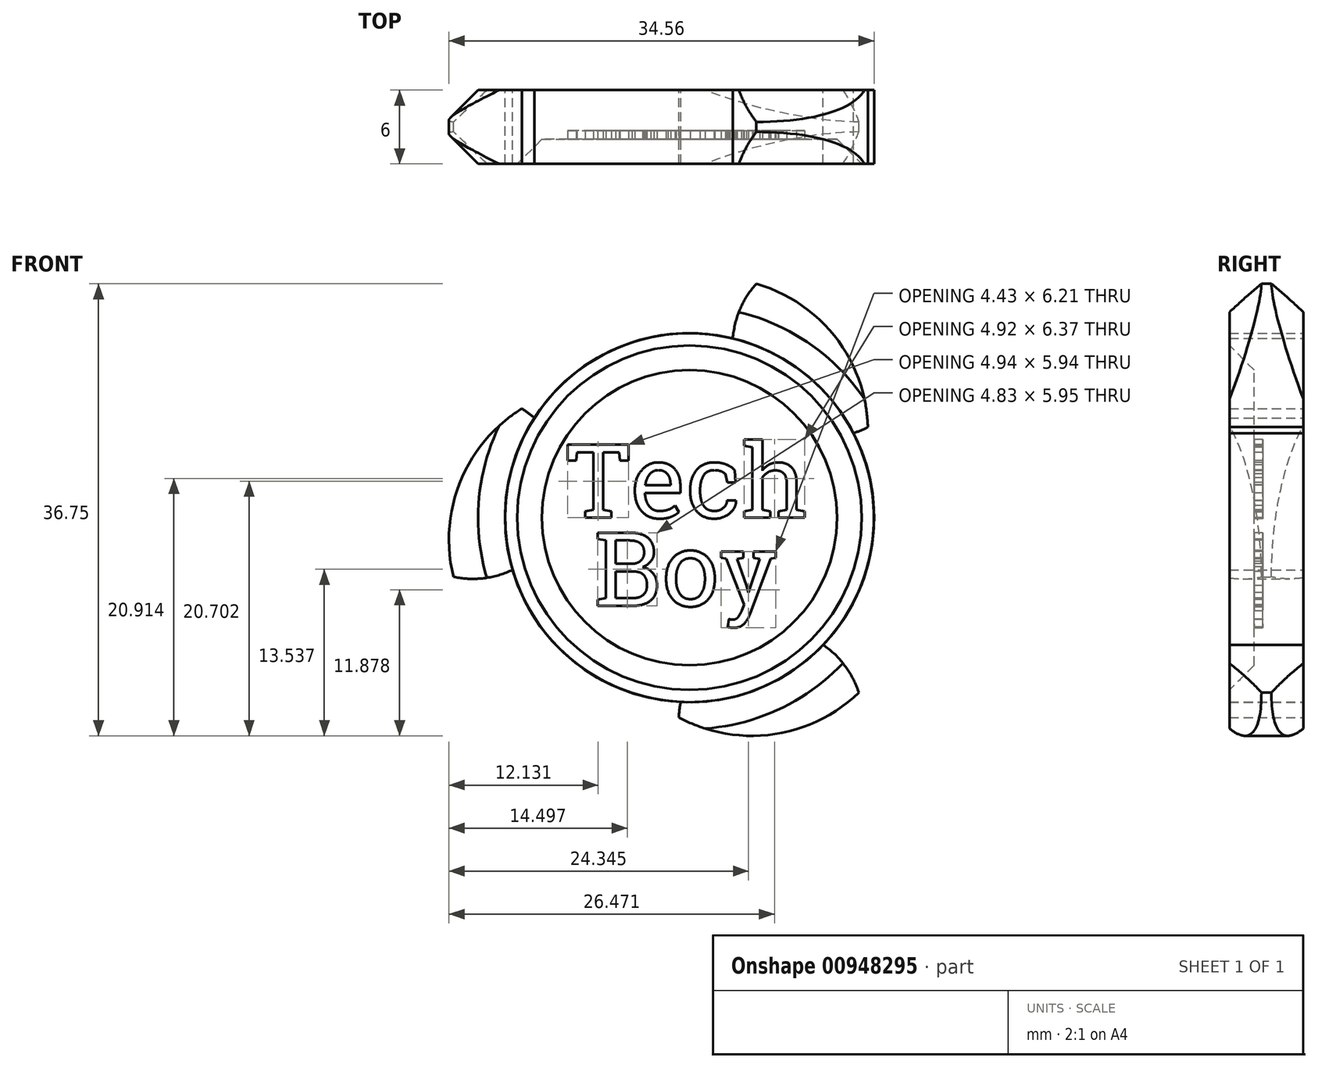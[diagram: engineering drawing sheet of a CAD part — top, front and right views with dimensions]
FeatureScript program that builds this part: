
annotation { "Feature Type Name" : "Feature", "Feature Type Description" : "" }
export const myFeature = defineFeature(function(context is Context, id is Id, definition is map)
    precondition{}
    {
        {
            var Q0;
            Q0=qCreatedBy(makeId("Front.planeOp"),FACE);
            var sketch = newSketch(context, id + "F0", { "sketchPlane" : qUnion([Q0])});
            skCircle(sketch, "E0", {"center": v(0, 0) * mm, "radius": 15 * mm});
            skSolve(sketch);
        }
        {
            var Q0;
            Q0=makeQuery(id+"F0.imprint","IMPRINT",FACE,{"disambiguationData":[TD([[makeQuery(id+"F0.imprint","IMPRINT",EDGE,{"derivedFrom":sQuery(id+"F0.wireOp",EDGE,"E0")}),1.0]])]});
            extrude(context, id + "F1", {"entities" : qUnion([Q0]), "depth" : 6 * mm, "offsetDistance" : 25.4 * mm});
        }
        {
            var Q0;
            Q0=qCreatedBy(makeId("Front.planeOp"),FACE);
            var sketch = newSketch(context, id + "F2", { "sketchPlane" : qUnion([Q0])});
            skCircle(sketch, "E1", {"center": v(2, 7) * mm, "radius": 12.5 * mm});
            skCircle(sketch, "E2", {"center": v(11, 14) * mm, "radius": 7.5 * mm});
            skCircle(sketch, "E3.0.0", {"center": v(0, 0) * mm, "radius": 15 * mm});
            skSolve(sketch);
        }
        {
            var Q0;
            {var subQ0=sQuery(id+"F2.wireOp",EDGE,"E2");var subQ1=sQuery(id+"F2.wireOp",EDGE,"E1");var subQ2=makeQuery(id+"F2.imprint","INTERSECT",VERTEX,{"disambiguationData":[OD(0.0)],"derivedFrom":[subQ1,subQ0]});Q0=makeQuery(id+"F2.imprint","IMPRINT",FACE,{"disambiguationData":[TD([[makeQuery(id+"F2.imprint","IMPRINT",EDGE,{"disambiguationData":[TD([[subQ2,-1.0]])],"derivedFrom":subQ1}),1.0]])]});}
            extrude(context, id + "F3", {"entities" : qUnion([Q0]), "operationType" : NewBodyOperationType.ADD, "depth" : 6 * mm, "offsetDistance" : 25.4 * mm});
        }
        {
            var Q0;
            Q0=makeQuery(id+"F1.opExtrude","SWEPT_BODY",BODY,{"disambiguationData":[OSD([sQuery(id+"F0.wireOp",EDGE,"E0")])]});
            var Q1;
            Q1=makeQuery(id+"F1.opExtrude","SWEPT_FACE",FACE,{"disambiguationData":[OSD([sQuery(id+"F0.wireOp",EDGE,"E0")])]});
            circularPattern(context, id + "F4", {"entities" : qUnion([Q0]), "axis" : qUnion([Q1]), "angle" : 360 * degree, "instanceCount" : 3, "equalSpace" : true});
        }
        {
            var Q0;
            Q0=makeQuery(id+"F4.opPattern","COPY",FACE,{"derivedFrom":makeQuery(id+"F3.boolean.opBoolean","MERGE",FACE,{"derivedFrom":[makeQuery(id+"F1.opExtrude","CAP_FACE",FACE,{"disambiguationData":[OSD([sQuery(id+"F0.wireOp",EDGE,"E0")])],"isStart":false}),makeQuery(id+"F3.opExtrude","CAP_FACE",FACE,{"disambiguationData":[OSD([sQuery(id+"F2.wireOp",EDGE,"E1"),sQuery(id+"F2.wireOp",EDGE,"E2"),sQuery(id+"F2.wireOp",EDGE,"E3.0.0")])],"isStart":false})]}),"instanceName":"2"});
            var sketch = newSketch(context, id + "F5", { "sketchPlane" : qUnion([Q0])});
            skCircle(sketch, "E4", {"center": v(0, 0) * mm, "radius": 14 * mm});
            skSolve(sketch);
        }
        {
            var Q0;
            Q0=makeQuery(id+"F5.imprint","IMPRINT",FACE,{"disambiguationData":[TD([[makeQuery(id+"F5.imprint","IMPRINT",EDGE,{"derivedFrom":sQuery(id+"F5.wireOp",EDGE,"E4")}),1.0]])]});
            extrude(context, id + "F6", {"entities" : qUnion([Q0]), "operationType" : NewBodyOperationType.REMOVE, "oppositeDirection" : true, "depth" : 2 * mm, "offsetDistance" : 25.4 * mm, "hasDraft" : true, "draftAngle" : 45 * degree, "draftPullDirection" : true});
        }
        {
            var Q0;
            Q0=qCreatedBy(makeId("Top.planeOp"),FACE);
            var sketch = newSketch(context, id + "F7", { "sketchPlane" : qUnion([Q0])});
            skPoint(sketch, "E5", {"position": v(-20.19, 0) * mm});
            skPoint(sketch, "E6", {"position": v(-20.19, -640778.1) * mm});
            skPoint(sketch, "E7", {"position": v(-19.19, -6) * mm});
            skPoint(sketch, "E8", {"position": v(-20.19, -6) * mm});
            skPoint(sketch, "E9", {"position": v(-20.19, -3) * mm});
            skPoint(sketch, "E10", {"position": v(-17.19, -6) * mm});
            skPoint(sketch, "E11", {"position": v(-17.19, 0) * mm});
            skLineSegment(sketch, "E12", {"start": v(-20.19, -3) * mm, "end": v(-17.19, 0) * mm});
            skLineSegment(sketch, "E13", {"start": v(-20.19, -3) * mm, "end": v(-17.19, -6) * mm});
            skLineSegment(sketch, "E14", {"start": v(-17.19, 0) * mm, "end": v(-24.5, 0) * mm});
            skLineSegment(sketch, "E15", {"start": v(-24.5, 0) * mm, "end": v(-24.5, -6) * mm});
            skLineSegment(sketch, "E16", {"start": v(-24.5, -6) * mm, "end": v(-17.19, -6) * mm});
            skSolve(sketch);
        }
        {
            var Q0;
            Q0=makeQuery(id+"F7.imprint","IMPRINT",FACE,{"disambiguationData":[TD([[makeQuery(id+"F7.imprint","IMPRINT",EDGE,{"derivedFrom":sQuery(id+"F7.wireOp",EDGE,"E12")}),1.0]])]});
            var Q1;
            Q1=makeQuery(id+"F4.opPattern","COPY",EDGE,{"derivedFrom":makeQuery(id+"F1.opExtrude","CAP_EDGE",EDGE,{"disambiguationData":[OSD([sQuery(id+"F0.wireOp",EDGE,"E0")])],"isStart":true}),"instanceName":"1"});
            revolve(context, id + "F8", {"operationType" : NewBodyOperationType.REMOVE, "surfaceOperationType" : NewSurfaceOperationType.NEW, "entities" : qUnion([Q0]), "axis" : qUnion([Q1]), "revolveType" : RevolveType.FULL, "oppositeDirection" : true});
        }
        {
            var Q0;
            Q0=makeQuery(id+"F5.imprint","IMPRINT",FACE,{"disambiguationData":[TD([[makeQuery(id+"F5.imprint","IMPRINT",EDGE,{"derivedFrom":sQuery(id+"F5.wireOp",EDGE,"E4")}),1.0]])]});
            var sketch = newSketch(context, id + "F9", { "sketchPlane" : qUnion([Q0])});
            skText(sketch, "E17", { "text": "Tech", "fontName": "RobotoSlab-Regular.ttf"});
            skText(sketch, "E18", { "text": "Boy", "fontName": "RobotoSlab-Regular.ttf"});
            const initialGuessF9  = {"E17": [-0.01005, 0, 1, 0, 0.00602], "E18": [-0.00777, -0.00717, 1, 0, 0.00603]};
            skSetInitialGuess(sketch, initialGuessF9);
            skSolve(sketch);
        }
        {
            var Q0;
            Q0 = qSketchRegion(id + "F9", true);
            extrude(context, id + "F10", {"entities" : qUnion([Q0]), "operationType" : NewBodyOperationType.REMOVE, "oppositeDirection" : true, "depth" : 2.7 * mm, "offsetDistance" : 25.4 * mm});
        }
    });
